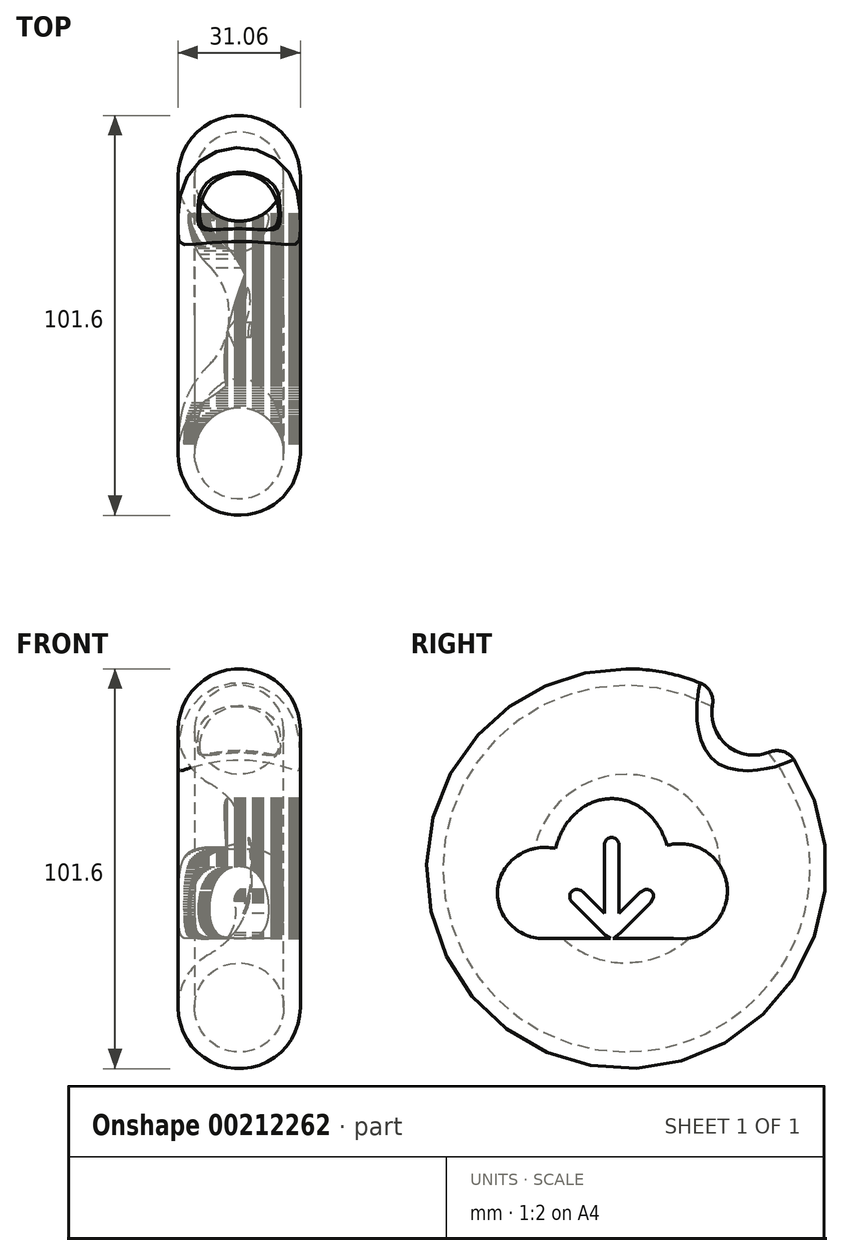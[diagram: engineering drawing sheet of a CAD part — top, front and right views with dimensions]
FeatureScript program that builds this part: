
annotation { "Feature Type Name" : "Feature", "Feature Type Description" : "" }
export const myFeature = defineFeature(function(context is Context, id is Id, definition is map)
    precondition{}
    {
        {
            var Q0;
            Q0=qCreatedBy(makeId("Top.planeOp"),FACE);
            var sketch = newSketch(context, id + "F0", { "sketchPlane" : qUnion([Q0])});
            skArc(sketch, "E0", {"start": v(10.16, -18.2) * mm, "mid": v(18.8, -9) * mm, "end": v(20.56, 3.5) * mm});
            skArc(sketch, "E1", {"start": v(10.16, -18.2) * mm, "mid": v(9.87, -45.16) * mm, "end": v(33.26, -31.77) * mm});
            skLineSegment(sketch, "E2", {"start": v(33.26, -4.3) * mm, "end": v(33.26, 3.5) * mm});
            skLineSegment(sketch, "E3", {"start": v(33.26, -4.3) * mm, "end": v(33.26, -31.77) * mm});
            skLineSegment(sketch, "E4", {"start": v(20.56, 3.5) * mm, "end": v(46.67, 3.5) * mm});
            skPoint(sketch, "E5.orphan", {"position": v(33.26, 20.85) * mm});
            skCircle(sketch, "E6", {"center": v(17.73, -31.77) * mm, "radius": 11.33 * mm});
            skSolve(sketch);
        }
        {
            var Q0;
            {var subQ1=sQuery(id+"F0.wireOp",EDGE,"E0");Q0=makeQuery(id+"F0.imprint","IMPRINT",FACE,{"disambiguationData":[TD([[makeQuery(id+"F0.imprint","IMPRINT",EDGE,{"derivedFrom":subQ1}),-1.0]])]});}
            var Q1;
            Q1=sQuery(id+"F0.wireOp",EDGE,"E4");
            revolve(context, id + "F1", {"entities" : qUnion([Q0]), "axis" : qUnion([Q1]), "revolveType" : RevolveType.FULL});
        }
        {
            var Q0;
            Q0=qCreatedBy(makeId("Right.planeOp"),FACE);
            var sketch = newSketch(context, id + "F2", { "sketchPlane" : qUnion([Q0])});
            skCircle(sketch, "E7", {"center": v(35.9, 39.54) * mm, "radius": 10.68 * mm});
            skSolve(sketch);
        }
        {
            var Q0;
            Q0=makeQuery(id+"F2.imprint","IMPRINT",FACE,{"disambiguationData":[TD([[makeQuery(id+"F2.imprint","IMPRINT",EDGE,{"derivedFrom":sQuery(id+"F2.wireOp",EDGE,"E7")}),1.0]])]});
            extrude(context, id + "F3", {"entities" : qUnion([Q0]), "operationType" : NewBodyOperationType.REMOVE, "depth" : 53.85 * mm});
        }
        {
            var Q0;
            Q0=makeQuery(id+"F3.boolean.opBoolean","INTERSECT",EDGE,{"derivedFrom":[makeQuery(id+"F1.opRevolve","SWEPT_FACE",FACE,{"disambiguationData":[OSD([sQuery(id+"F0.wireOp",EDGE,"E1")])]}),makeQuery(id+"F3.opExtrude","SWEPT_FACE",FACE,{"disambiguationData":[OSD([sQuery(id+"F2.wireOp",EDGE,"E7")])]})]});
            fillet(context, id + "F4", {"entities" : qUnion([Q0]), "radius" : 5.08 * mm, "tangentPropagation" : true, "allowEdgeOverflow" : false});
        }
        {
            var Q0;
            Q0=qCreatedBy(makeId("Right.planeOp"),FACE);
            var sketch = newSketch(context, id + "F5", { "sketchPlane" : qUnion([Q0])});
            skLineSegment(sketch, "E8", {"start": v(-6.98, 15.9) * mm, "end": v(-6.63, 16.1) * mm});
            skLineSegment(sketch, "E9", {"start": v(-6.63, 16.1) * mm, "end": v(-6.28, 16.3) * mm});
            skLineSegment(sketch, "E10", {"start": v(-6.28, 16.3) * mm, "end": v(-5.92, 16.48) * mm});
            skLineSegment(sketch, "E11", {"start": v(-5.92, 16.48) * mm, "end": v(-5.56, 16.65) * mm});
            skLineSegment(sketch, "E12", {"start": v(-5.56, 16.65) * mm, "end": v(-5.2, 16.8) * mm});
            skLineSegment(sketch, "E13", {"start": v(-5.2, 16.8) * mm, "end": v(-4.82, 16.95) * mm});
            skLineSegment(sketch, "E14", {"start": v(-4.82, 16.95) * mm, "end": v(-4.45, 17.09) * mm});
            skLineSegment(sketch, "E15", {"start": v(-4.45, 17.09) * mm, "end": v(-4.07, 17.21) * mm});
            skLineSegment(sketch, "E16", {"start": v(-4.07, 17.21) * mm, "end": v(-3.68, 17.32) * mm});
            skLineSegment(sketch, "E17", {"start": v(-3.68, 17.32) * mm, "end": v(-3.3, 17.43) * mm});
            skLineSegment(sketch, "E18", {"start": v(-3.3, 17.43) * mm, "end": v(-2.9, 17.51) * mm});
            skLineSegment(sketch, "E19", {"start": v(-2.9, 17.51) * mm, "end": v(-2.51, 17.6) * mm});
            skLineSegment(sketch, "E20", {"start": v(-2.51, 17.6) * mm, "end": v(-2.12, 17.66) * mm});
            skLineSegment(sketch, "E21", {"start": v(-2.12, 17.66) * mm, "end": v(-1.72, 17.71) * mm});
            skLineSegment(sketch, "E22", {"start": v(-1.72, 17.71) * mm, "end": v(-1.32, 17.75) * mm});
            skLineSegment(sketch, "E23", {"start": v(-1.32, 17.75) * mm, "end": v(-0.92, 17.78) * mm});
            skLineSegment(sketch, "E24", {"start": v(-0.92, 17.78) * mm, "end": v(-0.52, 17.8) * mm});
            skLineSegment(sketch, "E25", {"start": v(-0.52, 17.8) * mm, "end": v(-0.12, 17.8) * mm});
            skLineSegment(sketch, "E26", {"start": v(-0.12, 17.8) * mm, "end": v(0.28, 17.8) * mm});
            skLineSegment(sketch, "E27", {"start": v(0.28, 17.8) * mm, "end": v(0.68, 17.78) * mm});
            skLineSegment(sketch, "E28", {"start": v(0.68, 17.78) * mm, "end": v(1.08, 17.75) * mm});
            skLineSegment(sketch, "E29", {"start": v(1.08, 17.75) * mm, "end": v(1.47, 17.7) * mm});
            skLineSegment(sketch, "E30", {"start": v(1.47, 17.7) * mm, "end": v(1.87, 17.65) * mm});
            skLineSegment(sketch, "E31", {"start": v(1.87, 17.65) * mm, "end": v(2.26, 17.58) * mm});
            skLineSegment(sketch, "E32", {"start": v(2.26, 17.58) * mm, "end": v(2.66, 17.5) * mm});
            skLineSegment(sketch, "E33", {"start": v(2.66, 17.5) * mm, "end": v(3.05, 17.4) * mm});
            skLineSegment(sketch, "E34", {"start": v(3.05, 17.4) * mm, "end": v(3.43, 17.3) * mm});
            skLineSegment(sketch, "E35", {"start": v(3.43, 17.3) * mm, "end": v(3.82, 17.18) * mm});
            skLineSegment(sketch, "E36", {"start": v(3.82, 17.18) * mm, "end": v(4.2, 17.05) * mm});
            skLineSegment(sketch, "E37", {"start": v(4.2, 17.05) * mm, "end": v(4.7, 16.86) * mm});
            skLineSegment(sketch, "E38", {"start": v(4.7, 16.86) * mm, "end": v(5.18, 16.65) * mm});
            skLineSegment(sketch, "E39", {"start": v(5.18, 16.65) * mm, "end": v(5.66, 16.42) * mm});
            skLineSegment(sketch, "E40", {"start": v(5.66, 16.42) * mm, "end": v(6.13, 16.17) * mm});
            skLineSegment(sketch, "E41", {"start": v(6.13, 16.17) * mm, "end": v(6.58, 15.91) * mm});
            skLineSegment(sketch, "E42", {"start": v(6.58, 15.91) * mm, "end": v(7.03, 15.63) * mm});
            skLineSegment(sketch, "E43", {"start": v(7.03, 15.63) * mm, "end": v(7.46, 15.34) * mm});
            skLineSegment(sketch, "E44", {"start": v(7.46, 15.34) * mm, "end": v(7.88, 15.02) * mm});
            skLineSegment(sketch, "E45", {"start": v(7.88, 15.02) * mm, "end": v(8.3, 14.7) * mm});
            skLineSegment(sketch, "E46", {"start": v(8.3, 14.7) * mm, "end": v(8.7, 14.36) * mm});
            skLineSegment(sketch, "E47", {"start": v(8.7, 14.36) * mm, "end": v(9.08, 14) * mm});
            skLineSegment(sketch, "E48", {"start": v(9.08, 14) * mm, "end": v(9.46, 13.63) * mm});
            skLineSegment(sketch, "E49", {"start": v(9.46, 13.63) * mm, "end": v(9.82, 13.25) * mm});
            skLineSegment(sketch, "E50", {"start": v(9.82, 13.25) * mm, "end": v(10.17, 12.86) * mm});
            skLineSegment(sketch, "E51", {"start": v(10.17, 12.86) * mm, "end": v(10.51, 12.45) * mm});
            skLineSegment(sketch, "E52", {"start": v(10.51, 12.45) * mm, "end": v(10.84, 12.04) * mm});
            skLineSegment(sketch, "E53", {"start": v(10.84, 12.04) * mm, "end": v(11.15, 11.61) * mm});
            skLineSegment(sketch, "E54", {"start": v(11.15, 11.61) * mm, "end": v(11.46, 11.18) * mm});
            skLineSegment(sketch, "E55", {"start": v(11.46, 11.18) * mm, "end": v(11.74, 10.73) * mm});
            skLineSegment(sketch, "E56", {"start": v(11.74, 10.73) * mm, "end": v(12.02, 10.28) * mm});
            skLineSegment(sketch, "E57", {"start": v(12.02, 10.28) * mm, "end": v(12.28, 9.82) * mm});
            skLineSegment(sketch, "E58", {"start": v(12.28, 9.82) * mm, "end": v(12.53, 9.35) * mm});
            skLineSegment(sketch, "E59", {"start": v(12.53, 9.35) * mm, "end": v(12.76, 8.88) * mm});
            skLineSegment(sketch, "E60", {"start": v(12.76, 8.88) * mm, "end": v(12.98, 8.4) * mm});
            skLineSegment(sketch, "E61", {"start": v(12.98, 8.4) * mm, "end": v(13.19, 7.9) * mm});
            skLineSegment(sketch, "E62", {"start": v(13.19, 7.9) * mm, "end": v(13.38, 7.42) * mm});
            skLineSegment(sketch, "E63", {"start": v(13.38, 7.42) * mm, "end": v(13.56, 6.92) * mm});
            skLineSegment(sketch, "E64", {"start": v(13.56, 6.92) * mm, "end": v(13.72, 6.42) * mm});
            skLineSegment(sketch, "E65", {"start": v(13.72, 6.42) * mm, "end": v(13.87, 5.92) * mm});
            skLineSegment(sketch, "E66", {"start": v(13.87, 5.92) * mm, "end": v(14.25, 6.02) * mm});
            skLineSegment(sketch, "E67", {"start": v(14.25, 6.02) * mm, "end": v(14.63, 6.1) * mm});
            skLineSegment(sketch, "E68", {"start": v(14.63, 6.1) * mm, "end": v(15, 6.18) * mm});
            skLineSegment(sketch, "E69", {"start": v(15, 6.18) * mm, "end": v(15.4, 6.24) * mm});
            skLineSegment(sketch, "E70", {"start": v(15.4, 6.24) * mm, "end": v(15.78, 6.3) * mm});
            skLineSegment(sketch, "E71", {"start": v(15.78, 6.3) * mm, "end": v(16.17, 6.33) * mm});
            skLineSegment(sketch, "E72", {"start": v(16.17, 6.33) * mm, "end": v(16.56, 6.35) * mm});
            skLineSegment(sketch, "E73", {"start": v(16.56, 6.35) * mm, "end": v(16.94, 6.36) * mm});
            skLineSegment(sketch, "E74", {"start": v(16.94, 6.36) * mm, "end": v(17.33, 6.36) * mm});
            skLineSegment(sketch, "E75", {"start": v(17.33, 6.36) * mm, "end": v(17.72, 6.35) * mm});
            skLineSegment(sketch, "E76", {"start": v(17.72, 6.35) * mm, "end": v(18.11, 6.32) * mm});
            skLineSegment(sketch, "E77", {"start": v(18.11, 6.32) * mm, "end": v(18.5, 6.28) * mm});
            skLineSegment(sketch, "E78", {"start": v(18.5, 6.28) * mm, "end": v(18.88, 6.23) * mm});
            skLineSegment(sketch, "E79", {"start": v(18.88, 6.23) * mm, "end": v(19.27, 6.17) * mm});
            skLineSegment(sketch, "E80", {"start": v(19.27, 6.17) * mm, "end": v(19.65, 6.1) * mm});
            skLineSegment(sketch, "E81", {"start": v(19.65, 6.1) * mm, "end": v(20.03, 6.01) * mm});
            skLineSegment(sketch, "E82", {"start": v(20.03, 6.01) * mm, "end": v(20.4, 5.91) * mm});
            skLineSegment(sketch, "E83", {"start": v(20.4, 5.91) * mm, "end": v(20.78, 5.8) * mm});
            skLineSegment(sketch, "E84", {"start": v(20.78, 5.8) * mm, "end": v(21.15, 5.68) * mm});
            skLineSegment(sketch, "E85", {"start": v(21.15, 5.68) * mm, "end": v(21.51, 5.55) * mm});
            skLineSegment(sketch, "E86", {"start": v(21.51, 5.55) * mm, "end": v(21.87, 5.4) * mm});
            skLineSegment(sketch, "E87", {"start": v(21.87, 5.4) * mm, "end": v(22.23, 5.24) * mm});
            skLineSegment(sketch, "E88", {"start": v(22.23, 5.24) * mm, "end": v(22.58, 5.07) * mm});
            skLineSegment(sketch, "E89", {"start": v(22.58, 5.07) * mm, "end": v(22.92, 4.9) * mm});
            skLineSegment(sketch, "E90", {"start": v(22.92, 4.9) * mm, "end": v(23.26, 4.7) * mm});
            skLineSegment(sketch, "E91", {"start": v(23.26, 4.7) * mm, "end": v(23.59, 4.5) * mm});
            skLineSegment(sketch, "E92", {"start": v(23.59, 4.5) * mm, "end": v(23.91, 4.28) * mm});
            skLineSegment(sketch, "E93", {"start": v(23.91, 4.28) * mm, "end": v(24.23, 4.05) * mm});
            skLineSegment(sketch, "E94", {"start": v(24.23, 4.05) * mm, "end": v(24.54, 3.81) * mm});
            skLineSegment(sketch, "E95", {"start": v(24.54, 3.81) * mm, "end": v(24.82, 3.59) * mm});
            skLineSegment(sketch, "E96", {"start": v(24.82, 3.59) * mm, "end": v(25.1, 3.36) * mm});
            skLineSegment(sketch, "E97", {"start": v(25.1, 3.36) * mm, "end": v(25.36, 3.12) * mm});
            skLineSegment(sketch, "E98", {"start": v(25.36, 3.12) * mm, "end": v(25.62, 2.87) * mm});
            skLineSegment(sketch, "E99", {"start": v(25.62, 2.87) * mm, "end": v(25.87, 2.61) * mm});
            skLineSegment(sketch, "E100", {"start": v(25.87, 2.61) * mm, "end": v(26.11, 2.35) * mm});
            skLineSegment(sketch, "E101", {"start": v(26.11, 2.35) * mm, "end": v(26.35, 2.08) * mm});
            skLineSegment(sketch, "E102", {"start": v(26.35, 2.08) * mm, "end": v(26.57, 1.8) * mm});
            skLineSegment(sketch, "E103", {"start": v(26.57, 1.8) * mm, "end": v(26.8, 1.52) * mm});
            skLineSegment(sketch, "E104", {"start": v(26.8, 1.52) * mm, "end": v(27, 1.23) * mm});
            skLineSegment(sketch, "E105", {"start": v(27, 1.23) * mm, "end": v(27.2, 0.93) * mm});
            skLineSegment(sketch, "E106", {"start": v(27.2, 0.93) * mm, "end": v(27.4, 0.63) * mm});
            skLineSegment(sketch, "E107", {"start": v(27.4, 0.63) * mm, "end": v(27.58, 0.32) * mm});
            skLineSegment(sketch, "E108", {"start": v(27.58, 0.32) * mm, "end": v(27.75, 0.01) * mm});
            skLineSegment(sketch, "E109", {"start": v(27.75, 0.01) * mm, "end": v(27.92, -0.3) * mm});
            skLineSegment(sketch, "E110", {"start": v(27.92, -0.3) * mm, "end": v(28.08, -0.63) * mm});
            skLineSegment(sketch, "E111", {"start": v(28.08, -0.63) * mm, "end": v(28.22, -0.95) * mm});
            skLineSegment(sketch, "E112", {"start": v(28.22, -0.95) * mm, "end": v(28.36, -1.28) * mm});
            skLineSegment(sketch, "E113", {"start": v(28.36, -1.28) * mm, "end": v(28.49, -1.62) * mm});
            skLineSegment(sketch, "E114", {"start": v(28.49, -1.62) * mm, "end": v(28.6, -1.95) * mm});
            skLineSegment(sketch, "E115", {"start": v(28.6, -1.95) * mm, "end": v(28.71, -2.3) * mm});
            skLineSegment(sketch, "E116", {"start": v(28.71, -2.3) * mm, "end": v(28.81, -2.64) * mm});
            skLineSegment(sketch, "E117", {"start": v(28.81, -2.64) * mm, "end": v(28.9, -2.99) * mm});
            skLineSegment(sketch, "E118", {"start": v(28.9, -2.99) * mm, "end": v(28.98, -3.34) * mm});
            skLineSegment(sketch, "E119", {"start": v(28.98, -3.34) * mm, "end": v(29.04, -3.69) * mm});
            skLineSegment(sketch, "E120", {"start": v(29.04, -3.69) * mm, "end": v(29.1, -4.04) * mm});
            skLineSegment(sketch, "E121", {"start": v(29.1, -4.04) * mm, "end": v(29.14, -4.4) * mm});
            skLineSegment(sketch, "E122", {"start": v(29.14, -4.4) * mm, "end": v(29.18, -4.76) * mm});
            skLineSegment(sketch, "E123", {"start": v(29.18, -4.76) * mm, "end": v(29.2, -5.11) * mm});
            skLineSegment(sketch, "E124", {"start": v(29.2, -5.11) * mm, "end": v(29.2, -6.08) * mm});
            skLineSegment(sketch, "E125", {"start": v(29.2, -6.08) * mm, "end": v(29.18, -6.5) * mm});
            skLineSegment(sketch, "E126", {"start": v(29.18, -6.5) * mm, "end": v(29.15, -6.9) * mm});
            skLineSegment(sketch, "E127", {"start": v(29.15, -6.9) * mm, "end": v(29.1, -7.31) * mm});
            skLineSegment(sketch, "E128", {"start": v(29.1, -7.31) * mm, "end": v(29.05, -7.72) * mm});
            skLineSegment(sketch, "E129", {"start": v(29.05, -7.72) * mm, "end": v(28.97, -8.12) * mm});
            skLineSegment(sketch, "E130", {"start": v(28.97, -8.12) * mm, "end": v(28.88, -8.52) * mm});
            skLineSegment(sketch, "E131", {"start": v(28.88, -8.52) * mm, "end": v(28.78, -8.92) * mm});
            skLineSegment(sketch, "E132", {"start": v(28.78, -8.92) * mm, "end": v(28.66, -9.31) * mm});
            skLineSegment(sketch, "E133", {"start": v(28.66, -9.31) * mm, "end": v(28.53, -9.7) * mm});
            skLineSegment(sketch, "E134", {"start": v(28.53, -9.7) * mm, "end": v(28.39, -10.08) * mm});
            skLineSegment(sketch, "E135", {"start": v(28.39, -10.08) * mm, "end": v(28.23, -10.46) * mm});
            skLineSegment(sketch, "E136", {"start": v(28.23, -10.46) * mm, "end": v(28.06, -10.83) * mm});
            skLineSegment(sketch, "E137", {"start": v(28.06, -10.83) * mm, "end": v(27.88, -11.2) * mm});
            skLineSegment(sketch, "E138", {"start": v(27.88, -11.2) * mm, "end": v(27.69, -11.56) * mm});
            skLineSegment(sketch, "E139", {"start": v(27.69, -11.56) * mm, "end": v(27.48, -11.92) * mm});
            skLineSegment(sketch, "E140", {"start": v(27.48, -11.92) * mm, "end": v(27.27, -12.27) * mm});
            skLineSegment(sketch, "E141", {"start": v(27.27, -12.27) * mm, "end": v(27.04, -12.6) * mm});
            skLineSegment(sketch, "E142", {"start": v(27.04, -12.6) * mm, "end": v(26.8, -12.94) * mm});
            skLineSegment(sketch, "E143", {"start": v(26.8, -12.94) * mm, "end": v(26.55, -13.27) * mm});
            skLineSegment(sketch, "E144", {"start": v(26.55, -13.27) * mm, "end": v(26.29, -13.58) * mm});
            skLineSegment(sketch, "E145", {"start": v(26.29, -13.58) * mm, "end": v(26.02, -13.9) * mm});
            skLineSegment(sketch, "E146", {"start": v(26.02, -13.9) * mm, "end": v(25.74, -14.2) * mm});
            skLineSegment(sketch, "E147", {"start": v(25.74, -14.2) * mm, "end": v(25.45, -14.48) * mm});
            skLineSegment(sketch, "E148", {"start": v(25.45, -14.48) * mm, "end": v(25.15, -14.76) * mm});
            skLineSegment(sketch, "E149", {"start": v(25.15, -14.76) * mm, "end": v(24.84, -15.03) * mm});
            skLineSegment(sketch, "E150", {"start": v(24.84, -15.03) * mm, "end": v(24.52, -15.3) * mm});
            skLineSegment(sketch, "E151", {"start": v(24.52, -15.3) * mm, "end": v(24.2, -15.54) * mm});
            skLineSegment(sketch, "E152", {"start": v(24.2, -15.54) * mm, "end": v(23.86, -15.78) * mm});
            skLineSegment(sketch, "E153", {"start": v(23.86, -15.78) * mm, "end": v(23.52, -16) * mm});
            skLineSegment(sketch, "E154", {"start": v(23.52, -16) * mm, "end": v(23.28, -16.19) * mm});
            skLineSegment(sketch, "E155", {"start": v(23.28, -16.19) * mm, "end": v(23.04, -16.36) * mm});
            skLineSegment(sketch, "E156", {"start": v(23.04, -16.36) * mm, "end": v(22.8, -16.52) * mm});
            skLineSegment(sketch, "E157", {"start": v(22.8, -16.52) * mm, "end": v(22.55, -16.66) * mm});
            skLineSegment(sketch, "E158", {"start": v(22.55, -16.66) * mm, "end": v(22.3, -16.8) * mm});
            skLineSegment(sketch, "E159", {"start": v(22.3, -16.8) * mm, "end": v(22.04, -16.93) * mm});
            skLineSegment(sketch, "E160", {"start": v(22.04, -16.93) * mm, "end": v(21.77, -17.04) * mm});
            skLineSegment(sketch, "E161", {"start": v(21.77, -17.04) * mm, "end": v(21.5, -17.15) * mm});
            skLineSegment(sketch, "E162", {"start": v(21.5, -17.15) * mm, "end": v(20.97, -17.34) * mm});
            skLineSegment(sketch, "E163", {"start": v(20.97, -17.34) * mm, "end": v(20.41, -17.49) * mm});
            skLineSegment(sketch, "E164", {"start": v(20.41, -17.49) * mm, "end": v(19.85, -17.6) * mm});
            skLineSegment(sketch, "E165", {"start": v(19.85, -17.6) * mm, "end": v(18.98, -17.73) * mm});
            skLineSegment(sketch, "E166", {"start": v(18.98, -17.73) * mm, "end": v(17.82, -17.8) * mm});
            skLineSegment(sketch, "E167", {"start": v(17.82, -17.8) * mm, "end": v(15.5, -17.75) * mm});
            skLineSegment(sketch, "E168", {"start": v(15.5, -17.75) * mm, "end": v(0.13, -17.75) * mm});
            skLineSegment(sketch, "E169", {"start": v(0.13, -17.75) * mm, "end": v(0.22, -17.73) * mm});
            skLineSegment(sketch, "E170", {"start": v(0.22, -17.73) * mm, "end": v(2.1, -16.25) * mm});
            skLineSegment(sketch, "E171", {"start": v(2.1, -16.25) * mm, "end": v(9.63, -8.72) * mm});
            skLineSegment(sketch, "E172", {"start": v(9.63, -8.72) * mm, "end": v(10.46, -7.33) * mm});
            skLineSegment(sketch, "E173", {"start": v(10.46, -7.33) * mm, "end": v(10.47, -7.2) * mm});
            skLineSegment(sketch, "E174", {"start": v(10.47, -7.2) * mm, "end": v(10.48, -6.97) * mm});
            skLineSegment(sketch, "E175", {"start": v(10.48, -6.97) * mm, "end": v(10.46, -6.74) * mm});
            skLineSegment(sketch, "E176", {"start": v(10.46, -6.74) * mm, "end": v(10.4, -6.52) * mm});
            skLineSegment(sketch, "E177", {"start": v(10.4, -6.52) * mm, "end": v(10.31, -6.3) * mm});
            skLineSegment(sketch, "E178", {"start": v(10.31, -6.3) * mm, "end": v(10.14, -6) * mm});
            skLineSegment(sketch, "E179", {"start": v(10.14, -6) * mm, "end": v(9.91, -5.74) * mm});
            skLineSegment(sketch, "E180", {"start": v(9.91, -5.74) * mm, "end": v(9.64, -5.52) * mm});
            skLineSegment(sketch, "E181", {"start": v(9.64, -5.52) * mm, "end": v(9.34, -5.35) * mm});
            skLineSegment(sketch, "E182", {"start": v(9.34, -5.35) * mm, "end": v(9.12, -5.27) * mm});
            skLineSegment(sketch, "E183", {"start": v(9.12, -5.27) * mm, "end": v(8.9, -5.22) * mm});
            skLineSegment(sketch, "E184", {"start": v(8.9, -5.22) * mm, "end": v(8.66, -5.2) * mm});
            skLineSegment(sketch, "E185", {"start": v(8.66, -5.2) * mm, "end": v(8.43, -5.22) * mm});
            skLineSegment(sketch, "E186", {"start": v(8.43, -5.22) * mm, "end": v(6.95, -6.06) * mm});
            skLineSegment(sketch, "E187", {"start": v(6.95, -6.06) * mm, "end": v(1.7, -11.3) * mm});
            skLineSegment(sketch, "E188", {"start": v(1.7, -11.3) * mm, "end": v(1.7, 5.93) * mm});
            skLineSegment(sketch, "E189", {"start": v(1.7, 5.93) * mm, "end": v(1.7, 6.05) * mm});
            skLineSegment(sketch, "E190", {"start": v(1.7, 6.05) * mm, "end": v(1.7, 6.29) * mm});
            skLineSegment(sketch, "E191", {"start": v(1.7, 6.29) * mm, "end": v(1.65, 6.52) * mm});
            skLineSegment(sketch, "E192", {"start": v(1.65, 6.52) * mm, "end": v(1.57, 6.74) * mm});
            skLineSegment(sketch, "E193", {"start": v(1.57, 6.74) * mm, "end": v(1.47, 6.95) * mm});
            skLineSegment(sketch, "E194", {"start": v(1.47, 6.95) * mm, "end": v(1.28, 7.24) * mm});
            skLineSegment(sketch, "E195", {"start": v(1.28, 7.24) * mm, "end": v(1.03, 7.5) * mm});
            skLineSegment(sketch, "E196", {"start": v(1.03, 7.5) * mm, "end": v(0.75, 7.7) * mm});
            skLineSegment(sketch, "E197", {"start": v(0.75, 7.7) * mm, "end": v(0.44, 7.85) * mm});
            skLineSegment(sketch, "E198", {"start": v(0.44, 7.85) * mm, "end": v(0.21, 7.91) * mm});
            skLineSegment(sketch, "E199", {"start": v(0.21, 7.91) * mm, "end": v(-0.02, 7.95) * mm});
            skLineSegment(sketch, "E200", {"start": v(-0.02, 7.95) * mm, "end": v(-0.25, 7.95) * mm});
            skLineSegment(sketch, "E201", {"start": v(-0.25, 7.95) * mm, "end": v(-0.49, 7.91) * mm});
            skLineSegment(sketch, "E202", {"start": v(-0.49, 7.91) * mm, "end": v(-0.77, 7.85) * mm});
            skLineSegment(sketch, "E203", {"start": v(-0.77, 7.85) * mm, "end": v(-1.11, 7.7) * mm});
            skLineSegment(sketch, "E204", {"start": v(-1.11, 7.7) * mm, "end": v(-1.48, 7.41) * mm});
            skLineSegment(sketch, "E205", {"start": v(-1.48, 7.41) * mm, "end": v(-1.81, 6.96) * mm});
            skLineSegment(sketch, "E206", {"start": v(-1.81, 6.96) * mm, "end": v(-2, 6.44) * mm});
            skLineSegment(sketch, "E207", {"start": v(-2, 6.44) * mm, "end": v(-2.06, 5.97) * mm});
            skLineSegment(sketch, "E208", {"start": v(-2.06, 5.97) * mm, "end": v(-2.07, -11.34) * mm});
            skLineSegment(sketch, "E209", {"start": v(-2.07, -11.34) * mm, "end": v(-7.4, -6) * mm});
            skLineSegment(sketch, "E210", {"start": v(-7.4, -6) * mm, "end": v(-7.99, -5.5) * mm});
            skLineSegment(sketch, "E211", {"start": v(-7.99, -5.5) * mm, "end": v(-8.85, -5.2) * mm});
            skLineSegment(sketch, "E212", {"start": v(-8.85, -5.2) * mm, "end": v(-9.4, -5.25) * mm});
            skLineSegment(sketch, "E213", {"start": v(-9.4, -5.25) * mm, "end": v(-9.53, -5.28) * mm});
            skLineSegment(sketch, "E214", {"start": v(-9.53, -5.28) * mm, "end": v(-9.66, -5.32) * mm});
            skLineSegment(sketch, "E215", {"start": v(-9.66, -5.32) * mm, "end": v(-9.79, -5.38) * mm});
            skLineSegment(sketch, "E216", {"start": v(-9.79, -5.38) * mm, "end": v(-9.9, -5.44) * mm});
            skLineSegment(sketch, "E217", {"start": v(-9.9, -5.44) * mm, "end": v(-10.02, -5.5) * mm});
            skLineSegment(sketch, "E218", {"start": v(-10.02, -5.5) * mm, "end": v(-10.12, -5.58) * mm});
            skLineSegment(sketch, "E219", {"start": v(-10.12, -5.58) * mm, "end": v(-10.32, -5.76) * mm});
            skLineSegment(sketch, "E220", {"start": v(-10.32, -5.76) * mm, "end": v(-10.48, -5.97) * mm});
            skLineSegment(sketch, "E221", {"start": v(-10.48, -5.97) * mm, "end": v(-10.62, -6.2) * mm});
            skLineSegment(sketch, "E222", {"start": v(-10.62, -6.2) * mm, "end": v(-10.72, -6.44) * mm});
            skLineSegment(sketch, "E223", {"start": v(-10.72, -6.44) * mm, "end": v(-10.8, -6.7) * mm});
            skLineSegment(sketch, "E224", {"start": v(-10.8, -6.7) * mm, "end": v(-10.83, -6.96) * mm});
            skLineSegment(sketch, "E225", {"start": v(-10.83, -6.96) * mm, "end": v(-10.84, -7.22) * mm});
            skLineSegment(sketch, "E226", {"start": v(-10.84, -7.22) * mm, "end": v(-10.8, -7.49) * mm});
            skLineSegment(sketch, "E227", {"start": v(-10.8, -7.49) * mm, "end": v(-10.73, -7.74) * mm});
            skLineSegment(sketch, "E228", {"start": v(-10.73, -7.74) * mm, "end": v(-10.68, -7.86) * mm});
            skLineSegment(sketch, "E229", {"start": v(-10.68, -7.86) * mm, "end": v(-10.62, -7.98) * mm});
            skLineSegment(sketch, "E230", {"start": v(-10.62, -7.98) * mm, "end": v(-10.55, -8.1) * mm});
            skLineSegment(sketch, "E231", {"start": v(-10.55, -8.1) * mm, "end": v(-10.47, -8.2) * mm});
            skLineSegment(sketch, "E232", {"start": v(-10.47, -8.2) * mm, "end": v(-10.37, -8.3) * mm});
            skLineSegment(sketch, "E233", {"start": v(-10.37, -8.3) * mm, "end": v(-1.71, -17) * mm});
            skLineSegment(sketch, "E234", {"start": v(-1.71, -17) * mm, "end": v(-0.45, -17.76) * mm});
            skLineSegment(sketch, "E235", {"start": v(-0.45, -17.76) * mm, "end": v(-14.6, -17.74) * mm});
            skLineSegment(sketch, "E236", {"start": v(-14.6, -17.74) * mm, "end": v(-18.77, -17.72) * mm});
            skLineSegment(sketch, "E237", {"start": v(-18.77, -17.72) * mm, "end": v(-19.44, -17.61) * mm});
            skLineSegment(sketch, "E238", {"start": v(-19.44, -17.61) * mm, "end": v(-20.1, -17.47) * mm});
            skLineSegment(sketch, "E239", {"start": v(-20.1, -17.47) * mm, "end": v(-20.75, -17.3) * mm});
            skLineSegment(sketch, "E240", {"start": v(-20.75, -17.3) * mm, "end": v(-21.4, -17.07) * mm});
            skLineSegment(sketch, "E241", {"start": v(-21.4, -17.07) * mm, "end": v(-22.03, -16.82) * mm});
            skLineSegment(sketch, "E242", {"start": v(-22.03, -16.82) * mm, "end": v(-22.64, -16.54) * mm});
            skLineSegment(sketch, "E243", {"start": v(-22.64, -16.54) * mm, "end": v(-23.24, -16.22) * mm});
            skLineSegment(sketch, "E244", {"start": v(-23.24, -16.22) * mm, "end": v(-23.82, -15.87) * mm});
            skLineSegment(sketch, "E245", {"start": v(-23.82, -15.87) * mm, "end": v(-24.38, -15.49) * mm});
            skLineSegment(sketch, "E246", {"start": v(-24.38, -15.49) * mm, "end": v(-24.92, -15.08) * mm});
            skLineSegment(sketch, "E247", {"start": v(-24.92, -15.08) * mm, "end": v(-25.43, -14.64) * mm});
            skLineSegment(sketch, "E248", {"start": v(-25.43, -14.64) * mm, "end": v(-25.92, -14.16) * mm});
            skLineSegment(sketch, "E249", {"start": v(-25.92, -14.16) * mm, "end": v(-26.38, -13.67) * mm});
            skLineSegment(sketch, "E250", {"start": v(-26.38, -13.67) * mm, "end": v(-26.81, -13.14) * mm});
            skLineSegment(sketch, "E251", {"start": v(-26.81, -13.14) * mm, "end": v(-27.01, -12.87) * mm});
            skLineSegment(sketch, "E252", {"start": v(-27.01, -12.87) * mm, "end": v(-27.2, -12.6) * mm});
            skLineSegment(sketch, "E253", {"start": v(-27.2, -12.6) * mm, "end": v(-27.57, -12.05) * mm});
            skLineSegment(sketch, "E254", {"start": v(-27.57, -12.05) * mm, "end": v(-27.9, -11.48) * mm});
            skLineSegment(sketch, "E255", {"start": v(-27.9, -11.48) * mm, "end": v(-28.18, -10.9) * mm});
            skLineSegment(sketch, "E256", {"start": v(-28.18, -10.9) * mm, "end": v(-28.44, -10.29) * mm});
            skLineSegment(sketch, "E257", {"start": v(-28.44, -10.29) * mm, "end": v(-28.65, -9.67) * mm});
            skLineSegment(sketch, "E258", {"start": v(-28.65, -9.67) * mm, "end": v(-28.84, -9.04) * mm});
            skLineSegment(sketch, "E259", {"start": v(-28.84, -9.04) * mm, "end": v(-28.98, -8.4) * mm});
            skLineSegment(sketch, "E260", {"start": v(-28.98, -8.4) * mm, "end": v(-29.1, -7.76) * mm});
            skLineSegment(sketch, "E261", {"start": v(-29.1, -7.76) * mm, "end": v(-29.17, -7.1) * mm});
            skLineSegment(sketch, "E262", {"start": v(-29.17, -7.1) * mm, "end": v(-29.2, -6.45) * mm});
            skLineSegment(sketch, "E263", {"start": v(-29.2, -6.45) * mm, "end": v(-29.2, -5.8) * mm});
            skLineSegment(sketch, "E264", {"start": v(-29.2, -5.8) * mm, "end": v(-29.16, -5.14) * mm});
            skLineSegment(sketch, "E265", {"start": v(-29.16, -5.14) * mm, "end": v(-29.07, -4.5) * mm});
            skLineSegment(sketch, "E266", {"start": v(-29.07, -4.5) * mm, "end": v(-28.96, -3.85) * mm});
            skLineSegment(sketch, "E267", {"start": v(-28.96, -3.85) * mm, "end": v(-28.88, -3.52) * mm});
            skLineSegment(sketch, "E268", {"start": v(-28.88, -3.52) * mm, "end": v(-28.7, -2.89) * mm});
            skLineSegment(sketch, "E269", {"start": v(-28.7, -2.89) * mm, "end": v(-28.5, -2.27) * mm});
            skLineSegment(sketch, "E270", {"start": v(-28.5, -2.27) * mm, "end": v(-28.25, -1.66) * mm});
            skLineSegment(sketch, "E271", {"start": v(-28.25, -1.66) * mm, "end": v(-27.96, -1.07) * mm});
            skLineSegment(sketch, "E272", {"start": v(-27.96, -1.07) * mm, "end": v(-27.64, -0.5) * mm});
            skLineSegment(sketch, "E273", {"start": v(-27.64, -0.5) * mm, "end": v(-27.3, 0.06) * mm});
            skLineSegment(sketch, "E274", {"start": v(-27.3, 0.06) * mm, "end": v(-26.91, 0.6) * mm});
            skLineSegment(sketch, "E275", {"start": v(-26.91, 0.6) * mm, "end": v(-26.5, 1.11) * mm});
            skLineSegment(sketch, "E276", {"start": v(-26.5, 1.11) * mm, "end": v(-26.07, 1.6) * mm});
            skLineSegment(sketch, "E277", {"start": v(-26.07, 1.6) * mm, "end": v(-25.6, 2.07) * mm});
            skLineSegment(sketch, "E278", {"start": v(-25.6, 2.07) * mm, "end": v(-25.11, 2.51) * mm});
            skLineSegment(sketch, "E279", {"start": v(-25.11, 2.51) * mm, "end": v(-24.6, 2.92) * mm});
            skLineSegment(sketch, "E280", {"start": v(-24.6, 2.92) * mm, "end": v(-24.07, 3.3) * mm});
            skLineSegment(sketch, "E281", {"start": v(-24.07, 3.3) * mm, "end": v(-23.51, 3.66) * mm});
            skLineSegment(sketch, "E282", {"start": v(-23.51, 3.66) * mm, "end": v(-23.23, 3.82) * mm});
            skLineSegment(sketch, "E283", {"start": v(-23.23, 3.82) * mm, "end": v(-22.66, 4.13) * mm});
            skLineSegment(sketch, "E284", {"start": v(-22.66, 4.13) * mm, "end": v(-22.07, 4.4) * mm});
            skLineSegment(sketch, "E285", {"start": v(-22.07, 4.4) * mm, "end": v(-21.46, 4.65) * mm});
            skLineSegment(sketch, "E286", {"start": v(-21.46, 4.65) * mm, "end": v(-20.84, 4.85) * mm});
            skLineSegment(sketch, "E287", {"start": v(-20.84, 4.85) * mm, "end": v(-20.22, 5.03) * mm});
            skLineSegment(sketch, "E288", {"start": v(-20.22, 5.03) * mm, "end": v(-19.58, 5.18) * mm});
            skLineSegment(sketch, "E289", {"start": v(-19.58, 5.18) * mm, "end": v(-18.94, 5.29) * mm});
            skLineSegment(sketch, "E290", {"start": v(-18.94, 5.29) * mm, "end": v(-18.3, 5.37) * mm});
            skLineSegment(sketch, "E291", {"start": v(-18.3, 5.37) * mm, "end": v(-17.64, 5.41) * mm});
            skLineSegment(sketch, "E292", {"start": v(-17.64, 5.41) * mm, "end": v(-17, 5.42) * mm});
            skLineSegment(sketch, "E293", {"start": v(-17, 5.42) * mm, "end": v(-16.34, 5.4) * mm});
            skLineSegment(sketch, "E294", {"start": v(-16.34, 5.4) * mm, "end": v(-15.69, 5.35) * mm});
            skLineSegment(sketch, "E295", {"start": v(-15.69, 5.35) * mm, "end": v(-15.04, 5.26) * mm});
            skLineSegment(sketch, "E296", {"start": v(-15.04, 5.26) * mm, "end": v(-14.4, 5.14) * mm});
            skLineSegment(sketch, "E297", {"start": v(-14.4, 5.14) * mm, "end": v(-14.3, 5.59) * mm});
            skLineSegment(sketch, "E298", {"start": v(-14.3, 5.59) * mm, "end": v(-14.18, 6.03) * mm});
            skLineSegment(sketch, "E299", {"start": v(-14.18, 6.03) * mm, "end": v(-14.05, 6.48) * mm});
            skLineSegment(sketch, "E300", {"start": v(-14.05, 6.48) * mm, "end": v(-13.9, 6.92) * mm});
            skLineSegment(sketch, "E301", {"start": v(-13.9, 6.92) * mm, "end": v(-13.75, 7.35) * mm});
            skLineSegment(sketch, "E302", {"start": v(-13.75, 7.35) * mm, "end": v(-13.59, 7.79) * mm});
            skLineSegment(sketch, "E303", {"start": v(-13.59, 7.79) * mm, "end": v(-13.41, 8.22) * mm});
            skLineSegment(sketch, "E304", {"start": v(-13.41, 8.22) * mm, "end": v(-13.23, 8.64) * mm});
            skLineSegment(sketch, "E305", {"start": v(-13.23, 8.64) * mm, "end": v(-13.03, 9.06) * mm});
            skLineSegment(sketch, "E306", {"start": v(-13.03, 9.06) * mm, "end": v(-12.82, 9.47) * mm});
            skLineSegment(sketch, "E307", {"start": v(-12.82, 9.47) * mm, "end": v(-12.6, 9.88) * mm});
            skLineSegment(sketch, "E308", {"start": v(-12.6, 9.88) * mm, "end": v(-12.37, 10.28) * mm});
            skLineSegment(sketch, "E309", {"start": v(-12.37, 10.28) * mm, "end": v(-12.13, 10.68) * mm});
            skLineSegment(sketch, "E310", {"start": v(-12.13, 10.68) * mm, "end": v(-11.88, 11.07) * mm});
            skLineSegment(sketch, "E311", {"start": v(-11.88, 11.07) * mm, "end": v(-11.62, 11.45) * mm});
            skLineSegment(sketch, "E312", {"start": v(-11.62, 11.45) * mm, "end": v(-11.35, 11.83) * mm});
            skLineSegment(sketch, "E313", {"start": v(-11.35, 11.83) * mm, "end": v(-11.07, 12.2) * mm});
            skLineSegment(sketch, "E314", {"start": v(-11.07, 12.2) * mm, "end": v(-10.79, 12.56) * mm});
            skLineSegment(sketch, "E315", {"start": v(-10.79, 12.56) * mm, "end": v(-10.49, 12.9) * mm});
            skLineSegment(sketch, "E316", {"start": v(-10.49, 12.9) * mm, "end": v(-10.18, 13.25) * mm});
            skLineSegment(sketch, "E317", {"start": v(-10.18, 13.25) * mm, "end": v(-9.86, 13.59) * mm});
            skLineSegment(sketch, "E318", {"start": v(-9.86, 13.59) * mm, "end": v(-9.53, 13.91) * mm});
            skLineSegment(sketch, "E319", {"start": v(-9.53, 13.91) * mm, "end": v(-9.2, 14.23) * mm});
            skLineSegment(sketch, "E320", {"start": v(-9.2, 14.23) * mm, "end": v(-8.85, 14.53) * mm});
            skLineSegment(sketch, "E321", {"start": v(-8.85, 14.53) * mm, "end": v(-8.5, 14.83) * mm});
            skLineSegment(sketch, "E322", {"start": v(-8.5, 14.83) * mm, "end": v(-8.13, 15.11) * mm});
            skLineSegment(sketch, "E323", {"start": v(-8.13, 15.11) * mm, "end": v(-7.75, 15.38) * mm});
            skLineSegment(sketch, "E324", {"start": v(-7.75, 15.38) * mm, "end": v(-7.37, 15.65) * mm});
            skLineSegment(sketch, "E325", {"start": v(-7.37, 15.65) * mm, "end": v(-6.98, 15.9) * mm});
            skSolve(sketch);
        }
        {
            var Q0;
            Q0=makeQuery(id+"F5.imprint","IMPRINT",FACE,{"disambiguationData":[TD([[makeQuery(id+"F5.imprint","IMPRINT",EDGE,{"derivedFrom":sQuery(id+"F5.wireOp",EDGE,"E8")}),-1.0]])]});
            extrude(context, id + "F6", {"entities" : qUnion([Q0]), "operationType" : NewBodyOperationType.REMOVE, "depth" : 25.4 * mm});
        }
        {
            var Q0;
            Q0=qSketchRegion(id+"F5",true);
            extrude(context, id + "F7", {"entities" : qUnion([Q0]), "operationType" : NewBodyOperationType.REMOVE, "depth" : 50.8 * mm});
        }
    });
